# Revit family: Air-Curtain_Industrial_PoweredAire_Gas-Indirect-3Heater
name_source: partatom
category: Mechanical Equipment
revit_build: Autodesk Revit 2017 (Build: 20160225_1515(x64)
units: mm (PartAtom-declared; Revit-internal decimal feet)

## family parameters
Cut with Voids When Loaded = No
Host = Face
OmniClass Number = 23.75.35.17.21
OmniClass Title = Air Curtains
Part Type = Normal
Room Calculation Point = No
Round Connector Dimension = Use Diameter
Shared = No

## types (5) — shared parameters
Assembly Code = D3090400
Construction Details = http://www.arcat.com
Default Elevation = 0' - 0"
Exhaust Connection Diameter = 0' - 6"
Green Building-LEED = http://www.arcat.com
HVAC_BTU Input = 350000.0 Btu/h
HVAC_BTU Output = 840000.0 Btu/h
HVAC_Primary CFM = 0 CFM
Heater Hanging Width = 4' - 0 5/8"
Heating Element Load = 0 W
Keynote = 23 34 33
Manufacturer = Powered Aire, Inc
Manufacturer Fax = 724-588-3371
Manufacturer Website = http://www.poweredaire.com
Motor RPM = 1160
Overall Depth = 6' - 7 3/4"
Power Rating = 0 W
Product Data = http://www.arcat.com
Revision = R1_2016-08
Sales Information = http://www.poweredaire.com
Specification = http://www.arcat.com
Standards Conformance = AGA  ;  Made in USA
URL = http://www.poweredaire.com
Unit Depth = 2' - 3 1/4"
Unit Height = 1' - 9"
Unit Width Notes = Other Widths available.
zero-valued in all types: Expected Lifespan (Years), Heater Weight, Maintenance Schedule (Months), Warranty Duration (Years)

## per-type parameters (varying)
| type | Description | HVAC_Outlet Velocity | HVAC_Outlet Velocity Uniformity | HVAC_Outlet Volume | HVAC_Temperature Rise | Max Height | Model | Motor Count | Motor HP | Mounting Width | Nozzle Width | Sound Pressure | Unit Weight | Unit Width |
| 22 ft Opening EHD 240'' Nozzle | Powered Aire Indirect Gas Heated Industrial Air Curtain - EHD-4-240IG as Specified | 4400 FPM | 0.95 | 29100 CFM | 27 °F | 22' - 0" | EHD-4-240IG | 4 | 5 | 20' - 1 7/8" | 20' - 0 3/8" | >71 dBA | 2870 | 20' - 3 3/8" |
| 22 ft Opening EHD 228'' Nozzle | Powered Aire Indirect Gas Heated Industrial Air Curtain - EHD-4-228IG as Specified | 4800 FPM | 0.94 | 28300 CFM | 27 °F | 22' - 0" | EHD-4-228IG | 4 | 5 | 19' - 1 7/8" | 19' - 0 3/8" | >71 dBA | 2800 | 19' - 3 3/8" |
| 17 ft Opening TSD 240'' Nozzle 5 Motor | Powered Aire Indirect Gas Heated Industrial Air Curtain - TSD-5-240IG as Specified | 3900 FPM | 0.951 | 25900 CFM | 34 °F | 17' - 0" | TSD-5-240IG | 5 | 3 | 20' - 2" | 20' - 0 1/2" | >69 dBA | 2550 | 20' - 3 1/2" |
| 17 ft Opening TSD 240'' Nozzle 4 Motor | Powered Aire Indirect Gas Heated Industrial Air Curtain - TSD-4-240IG as Specified | 3300 FPM | 0.863 | 21500 CFM | 38 °F | 17' - 0" | TSD-4-240IG | 4 | 3 | 20' - 1 7/8" | 20' - 0 3/8" | >69 dBA | 2330 | 20' - 3 3/8" |
| 17 ft Opening TSD 228'' Nozzle | Powered Aire Indirect Gas Heated Industrial Air Curtain - TSD-4-228IG as Specified | 3300 FPM | 0.863 | 20800 CFM | 40 °F | 17' - 0" | TSD-4-228IG | 4 | 3 | 19' - 1 7/8" | 19' - 0 3/8" | >69 dBA | 2310 | 19' - 3 3/8" |

## geometry (parser evidence)
native form markers: Sweep x9
no freeform markers — native parametric forms only
